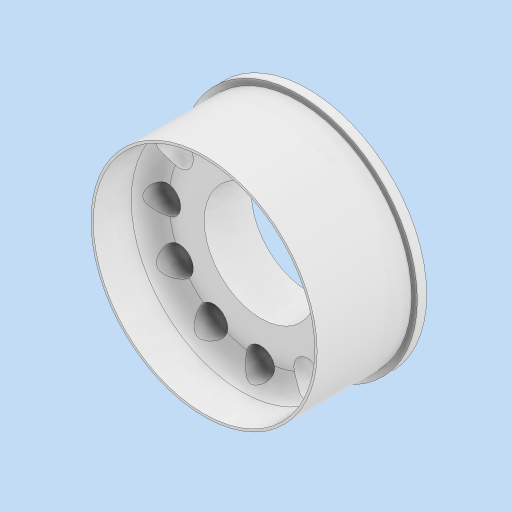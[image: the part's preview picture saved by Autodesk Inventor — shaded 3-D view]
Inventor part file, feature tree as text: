
AUTODESK INVENTOR PART (.ipt)
format: ipt  version: 2023 (Build 270158000, 158)  size: 239,616 bytes
history: native  units: in
note: dims shown in document units (in); Inventor stores cm internally (conversion verified against a paired STEP export)
features: extrude x4, sketch x1, pattern_circular x1, fillet x1
ambient origin geometry x8: Origin, YZ Plane, XZ Plane, XY Plane, X Axis, Y Axis, Z Axis, Center Point
bodies: Solid1 (feature_tree)
feature tree (7):
  sketch  "Sketch1"  dims[d0=3.0in d1=0.0315in d2=1.253in d3=0.0in d4=1.5in d5=0.5in d6=0.0in d7=2.5in d8=0.375in d9=0.5in d10=0.0in d11=4.7244in d12=360.0deg d14=0.25in d15=0.075in d16=0.125in d17=0.0in]
  extrude  "Extrusion1"  Depth=0.25in
  extrude  "Extrusion2"  Depth=0.25in TaperAngle=0.0deg
  extrude  "Extrusion4"  Depth=0.25in
  extrude  "Extrusion3"  Depth=0.25in TaperAngle=0.0deg
  pattern_circular  "Circular Pattern1"  [2 undecoded]
  fillet  "Fillet1"  Radius=0.375in
note: 2 required parameter values undecoded (feature->parameter linkage not recoverable at this tier; creation-order binding heuristic only, values carry confidence <= 0.55)
